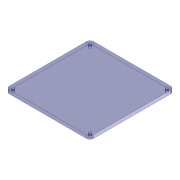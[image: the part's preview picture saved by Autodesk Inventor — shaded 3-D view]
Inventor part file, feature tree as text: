
AUTODESK INVENTOR PART (.ipt)
format: ipt  version: 2020 (Build 240168000, 168)  size: 108,032 bytes
history: native  units: mm
features: sketch x3, extrude x2, fillet x1
ambient origin geometry x8: Origin, YZ Plane, XZ Plane, XY Plane, X Axis, Y Axis, Z Axis, Center Point
bodies: Solid1 (feature_tree)
feature tree (6):
  extrude  "Extrusion1"  Depth=120.0mm
  extrude  "Extrusion2"  Depth=5.0mm
  fillet  "Fillet1"  Radius=110.0mm
  sketch  "Sketch3"  dims[d6=4.0mm d7=4.0mm d8=4.0mm d9=4.0mm d10=5.0mm d11=0.0mm d12=5.0mm d13=15.0mm]
  sketch  "Sketch1"  dims[d0=120.0mm d1=120.0mm]
  sketch  "Sketch2"  dims[d2=5.0mm d3=0.0mm d4=110.0mm d5=110.0mm]
